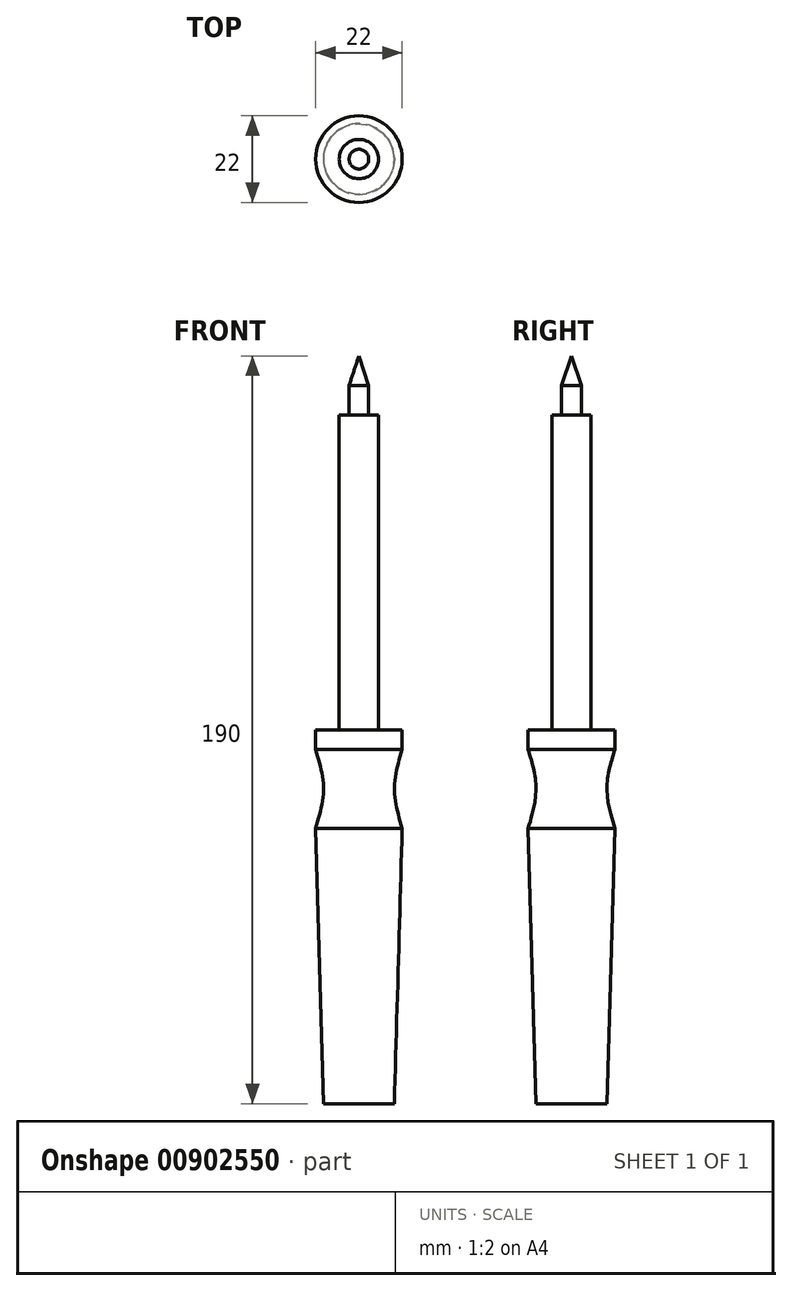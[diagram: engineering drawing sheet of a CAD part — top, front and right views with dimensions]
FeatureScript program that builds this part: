
annotation { "Feature Type Name" : "Feature", "Feature Type Description" : "" }
export const myFeature = defineFeature(function(context is Context, id is Id, definition is map)
    precondition{}
    {
        {
            var Q0;
            Q0=qCreatedBy(makeId("Top.planeOp"),FACE);
            var sketch = newSketch(context, id + "F0", { "sketchPlane" : qUnion([Q0])});
            skCircle(sketch, "E0", {"center": v(0, 0) * mm, "radius": 9 * mm});
            skSolve(sketch);
        }
        {
            var Q0;
            Q0=qCreatedBy(makeId("Top.planeOp"),FACE);
            cPlane(context, id + "F1", {"entities" : qUnion([Q0]), "cplaneType" : CPlaneType.OFFSET, "offset" : 70 * mm, "width" : 150 * mm, "height" : 150 * mm});
        }
        {
            var Q0;
            Q0=qCreatedBy(id+"F1.planeOp",FACE);
            var sketch = newSketch(context, id + "F2", { "sketchPlane" : qUnion([Q0])});
            skCircle(sketch, "E1", {"center": v(0, 0) * mm, "radius": 11 * mm});
            skSolve(sketch);
        }
        {
            var Q0;
            Q0=qCreatedBy(id+"F1.planeOp",FACE);
            cPlane(context, id + "F3", {"entities" : qUnion([Q0]), "cplaneType" : CPlaneType.OFFSET, "offset" : 10 * mm, "width" : 150 * mm, "height" : 150 * mm});
        }
        {
            var Q0;
            Q0=qCreatedBy(id+"F3.planeOp",FACE);
            var sketch = newSketch(context, id + "F4", { "sketchPlane" : qUnion([Q0])});
            skCircle(sketch, "E2", {"center": v(0, 0) * mm, "radius": 9 * mm});
            skSolve(sketch);
        }
        {
            var Q0;
            Q0=qCreatedBy(id+"F3.planeOp",FACE);
            cPlane(context, id + "F5", {"entities" : qUnion([Q0]), "cplaneType" : CPlaneType.OFFSET, "offset" : 10 * mm, "width" : 150 * mm, "height" : 150 * mm});
        }
        {
            var Q0;
            Q0=qCreatedBy(id+"F5.planeOp",FACE);
            var sketch = newSketch(context, id + "F6", { "sketchPlane" : qUnion([Q0])});
            skCircle(sketch, "E3", {"center": v(0, 0) * mm, "radius": 11 * mm});
            skSolve(sketch);
        }
        {
            var Q0;
            Q0=makeQuery(id+"F0.imprint","IMPRINT",FACE,{"disambiguationData":[TD([[makeQuery(id+"F0.imprint","IMPRINT",EDGE,{"derivedFrom":sQuery(id+"F0.wireOp",EDGE,"E0")}),1.0]])]});
            var Q1;
            Q1=makeQuery(id+"F2.imprint","IMPRINT",FACE,{"disambiguationData":[TD([[makeQuery(id+"F2.imprint","IMPRINT",EDGE,{"derivedFrom":sQuery(id+"F2.wireOp",EDGE,"E1")}),1.0]])]});
            loft(context, id + "F7", {"sheetProfilesArray" : [{ "sheetProfileEntities" : qUnion([Q0]) }, { "sheetProfileEntities" : qUnion([Q1]) }]});
        }
        {
            var Q1;
            Q1=makeQuery(id+"F7.opLoft","CAP_FACE",FACE,{"disambiguationData":[OSD([makeQuery(id+"F2.imprint","IMPRINT",FACE,{"disambiguationData":[TD([[makeQuery(id+"F2.imprint","IMPRINT",EDGE,{"derivedFrom":sQuery(id+"F2.wireOp",EDGE,"E1")}),1.0]])]})])],"isStart":true});
            var Q2;
            Q2=makeQuery(id+"F4.imprint","IMPRINT",FACE,{"disambiguationData":[TD([[makeQuery(id+"F4.imprint","IMPRINT",EDGE,{"derivedFrom":sQuery(id+"F4.wireOp",EDGE,"E2")}),1.0]])]});
            var Q3;
            Q3=makeQuery(id+"F6.imprint","IMPRINT",FACE,{"disambiguationData":[TD([[makeQuery(id+"F6.imprint","IMPRINT",EDGE,{"derivedFrom":sQuery(id+"F6.wireOp",EDGE,"E3")}),1.0]])]});
            loft(context, id + "F8", {"operationType" : NewBodyOperationType.ADD, "sheetProfilesArray" : [{ "sheetProfileEntities" : qUnion([Q1]) }, { "sheetProfileEntities" : qUnion([Q2]) }, { "sheetProfileEntities" : qUnion([Q3]) }]});
        }
        {
            var Q0;
            Q0=makeQuery(id+"F8.opLoft","CAP_FACE",FACE,{"disambiguationData":[OSD([makeQuery(id+"F6.imprint","IMPRINT",FACE,{"disambiguationData":[TD([[makeQuery(id+"F6.imprint","IMPRINT",EDGE,{"derivedFrom":sQuery(id+"F6.wireOp",EDGE,"E3")}),1.0]])]})])],"isStart":true});
            extrude(context, id + "F9", {"entities" : qUnion([Q0]), "operationType" : NewBodyOperationType.ADD, "depth" : 5 * mm, "offsetDistance" : 25 * mm});
        }
        {
            var Q0;
            Q0=makeQuery(id+"F9.opExtrude","CAP_FACE",FACE,{"disambiguationData":[OSD([makeQuery(id+"F6.imprint","IMPRINT",FACE,{"disambiguationData":[TD([[makeQuery(id+"F6.imprint","IMPRINT",EDGE,{"derivedFrom":sQuery(id+"F6.wireOp",EDGE,"E3")}),1.0]])]})])],"isStart":false});
            var sketch = newSketch(context, id + "F10", { "sketchPlane" : qUnion([Q0])});
            skCircle(sketch, "E4", {"center": v(0, 0) * mm, "radius": 5 * mm});
            skSolve(sketch);
        }
        {
            var Q0;
            Q0=makeQuery(id+"F10.imprint","IMPRINT",FACE,{"disambiguationData":[TD([[makeQuery(id+"F10.imprint","IMPRINT",EDGE,{"derivedFrom":sQuery(id+"F10.wireOp",EDGE,"E4")}),1.0]])]});
            extrude(context, id + "F11", {"entities" : qUnion([Q0]), "depth" : 80 * mm, "offsetDistance" : 25 * mm});
        }
        {
            var Q0;
            Q0=makeQuery(id+"F11.opExtrude","CAP_FACE",FACE,{"disambiguationData":[OSD([sQuery(id+"F10.wireOp",EDGE,"E4")])],"isStart":false});
            var sketch = newSketch(context, id + "F12", { "sketchPlane" : qUnion([Q0])});
            skCircle(sketch, "E5", {"center": v(0, 0) * mm, "radius": 2.5 * mm});
            skSolve(sketch);
        }
        {
            var Q0;
            Q0=makeQuery(id+"F12.imprint","IMPRINT",FACE,{"disambiguationData":[TD([[makeQuery(id+"F12.imprint","IMPRINT",EDGE,{"derivedFrom":sQuery(id+"F12.wireOp",EDGE,"E5")}),1.0]])]});
            extrude(context, id + "F13", {"entities" : qUnion([Q0]), "operationType" : NewBodyOperationType.ADD, "depth" : 15 * mm, "offsetDistance" : 25 * mm});
        }
        {
            var Q0;
            Q0=makeQuery(id+"F13.opExtrude","CAP_EDGE",EDGE,{"disambiguationData":[OSD([sQuery(id+"F12.wireOp",EDGE,"E5")])],"isStart":false});
            chamfer(context, id + "F14", {"entities" : qUnion([Q0]), "chamferType" : ChamferType.TWO_OFFSETS, "width1" : 2.5 * mm, "oppositeDirection" : false, "width2" : 7.5 * mm, "tangentPropagation" : true});
        }
    });
